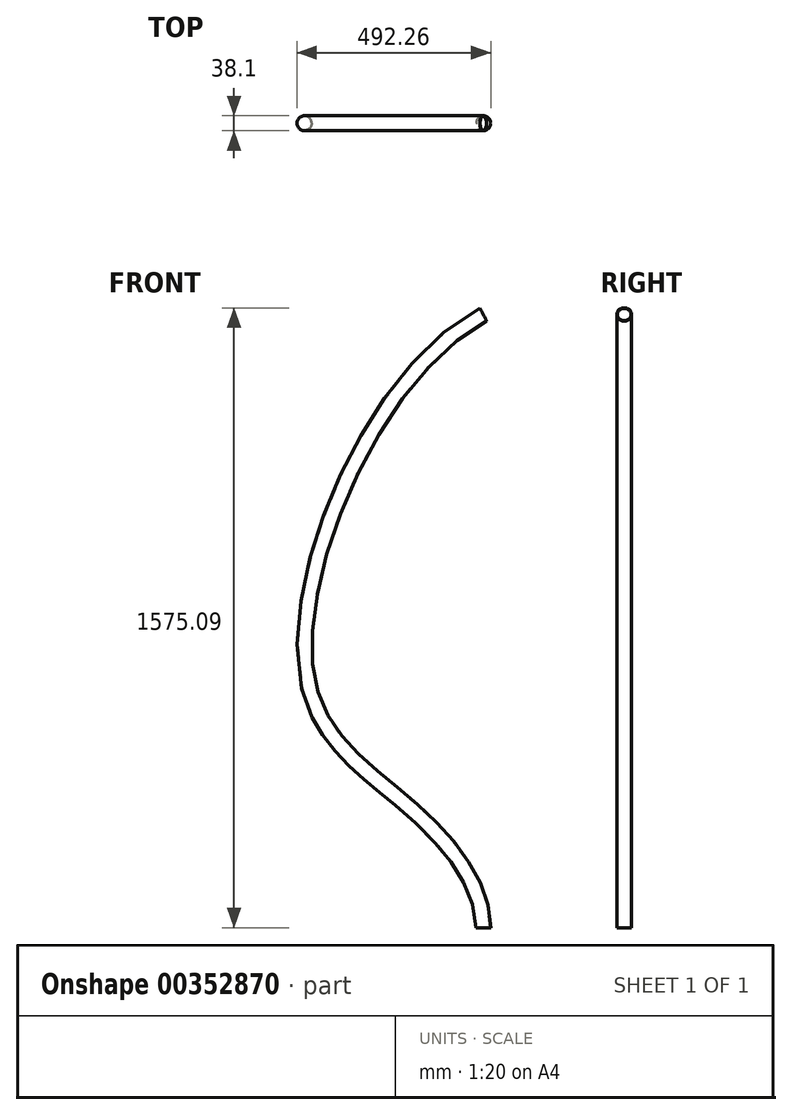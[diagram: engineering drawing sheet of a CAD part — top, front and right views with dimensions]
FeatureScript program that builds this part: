
annotation { "Feature Type Name" : "Feature", "Feature Type Description" : "" }
export const myFeature = defineFeature(function(context is Context, id is Id, definition is map)
    precondition{}
    {
        {
            var Q0;
            Q0=qCreatedBy(makeId("Front.planeOp"),FACE);
            var sketch = newSketch(context, id + "F0", { "sketchPlane" : qUnion([Q0])});
            skFitSpline(sketch, "E0", {"points": [v(0, 0) * mm, v(-180.68, 300) * mm, v(-450, 650) * mm, v(0, 1558.2) * mm], "startDerivative": vector(0, 1236.95) * mm, "endDerivative": vector(1841.35, 959.58) * mm});
            skSolve(sketch);
        }
        {
            var Q0;
            Q0=qCreatedBy(makeId("Top.planeOp"),FACE);
            var sketch = newSketch(context, id + "F1", { "sketchPlane" : qUnion([Q0])});
            skCircle(sketch, "E1", {"center": v(0, 0) * mm, "radius": 19.05 * mm});
            skCircle(sketch, "E2", {"center": v(0, 0) * mm, "radius": 17.5 * mm});
            skSolve(sketch);
        }
        {
            var Q0;
            Q0=makeQuery(id+"F1.imprint","IMPRINT",FACE,{"disambiguationData":[TD([[makeQuery(id+"F1.imprint","IMPRINT",EDGE,{"derivedFrom":sQuery(id+"F1.wireOp",EDGE,"E1")}),1.0]])]});
            var Q1;
            Q1=sQuery(id+"F0.wireOp",EDGE,"E0");
            sweep(context, id + "F2", {"profiles" : qUnion([Q0]), "path" : qUnion([Q1])});
        }
    });
